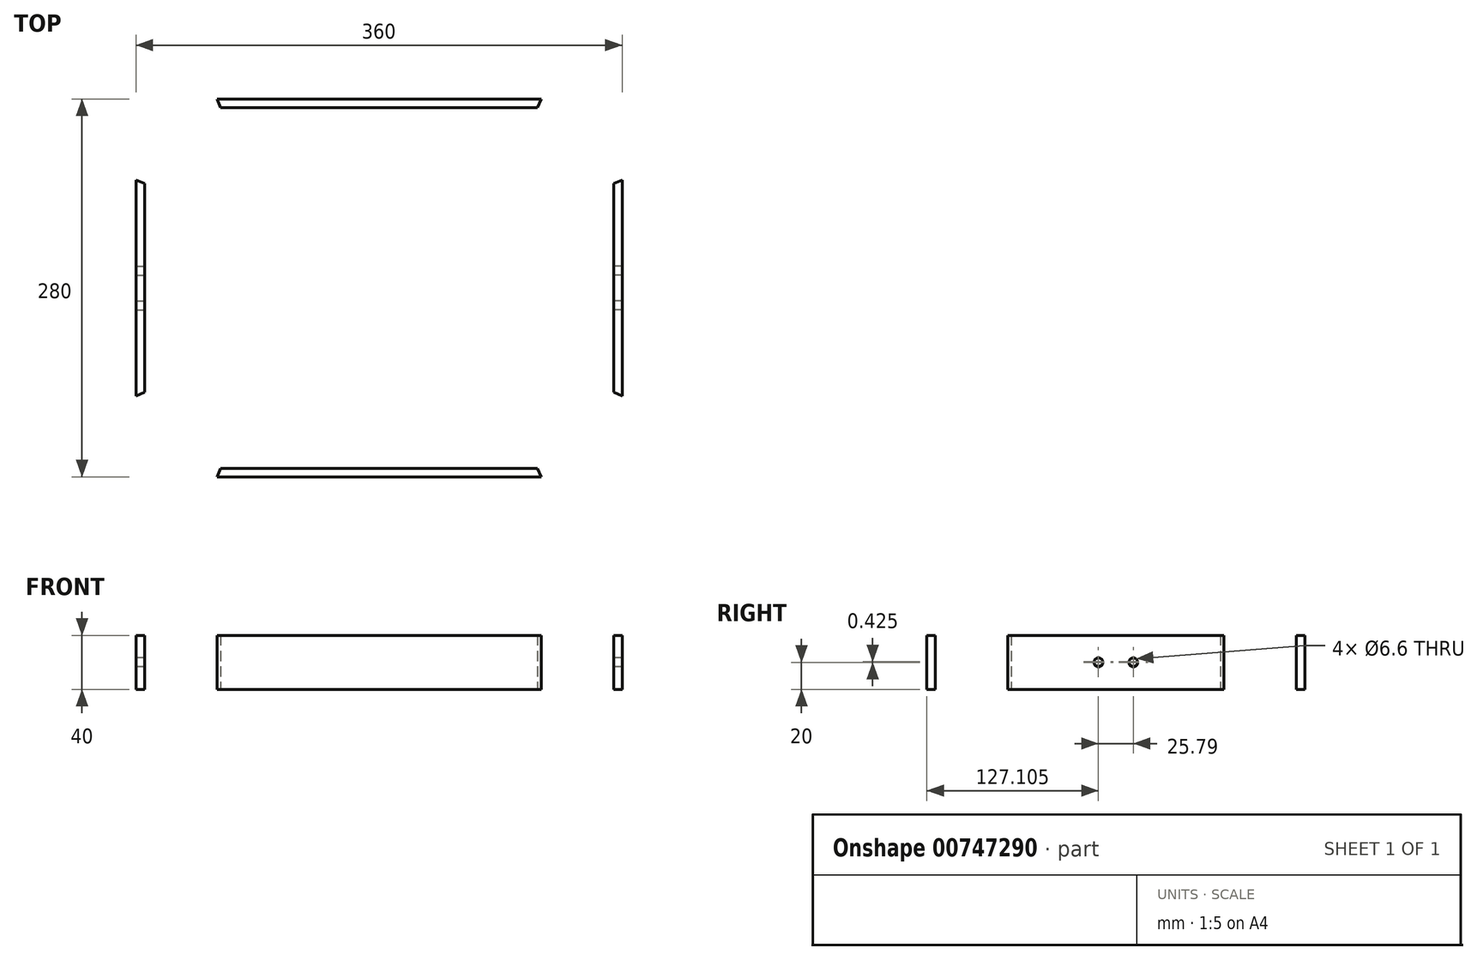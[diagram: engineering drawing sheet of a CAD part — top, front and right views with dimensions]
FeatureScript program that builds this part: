
annotation { "Feature Type Name" : "Feature", "Feature Type Description" : "" }
export const myFeature = defineFeature(function(context is Context, id is Id, definition is map)
    precondition{}
    {
        {
            var Q0;
            Q0=qCreatedBy(makeId("Top.planeOp"),FACE);
            var sketch = newSketch(context, id + "F0", { "sketchPlane" : qUnion([Q0])});
            skLineSegment(sketch, "E0", {"start": v(-120, 0) * mm, "end": v(-180, 60) * mm});
            skLineSegment(sketch, "E1", {"start": v(-180, 60) * mm, "end": v(-180, 220) * mm});
            skLineSegment(sketch, "E2", {"start": v(-180, 220) * mm, "end": v(-120, 280) * mm});
            skLineSegment(sketch, "E3", {"start": v(-120, 280) * mm, "end": v(120, 280) * mm});
            skLineSegment(sketch, "E4", {"start": v(120, 280) * mm, "end": v(180, 220) * mm});
            skLineSegment(sketch, "E5", {"start": v(180, 220) * mm, "end": v(180, 60) * mm});
            skLineSegment(sketch, "E6", {"start": v(180, 60) * mm, "end": v(120, 0) * mm});
            skLineSegment(sketch, "E7", {"start": v(120, 0) * mm, "end": v(-120, 0) * mm});
            skLineSegment(sketch, "E8.0", {"start": v(-173.65, 62.63) * mm, "end": v(-173.65, 217.37) * mm});
            skLineSegment(sketch, "E8.1", {"start": v(-117.37, 6.35) * mm, "end": v(-173.65, 62.63) * mm});
            skLineSegment(sketch, "E8.2", {"start": v(-173.65, 217.37) * mm, "end": v(-117.37, 273.65) * mm});
            skLineSegment(sketch, "E8.3", {"start": v(117.37, 6.35) * mm, "end": v(-117.37, 6.35) * mm});
            skLineSegment(sketch, "E8.4", {"start": v(-117.37, 273.65) * mm, "end": v(117.37, 273.65) * mm});
            skLineSegment(sketch, "E8.5", {"start": v(117.37, 273.65) * mm, "end": v(173.65, 217.37) * mm});
            skLineSegment(sketch, "E8.6", {"start": v(173.65, 217.37) * mm, "end": v(173.65, 62.63) * mm});
            skLineSegment(sketch, "E8.7", {"start": v(173.65, 62.63) * mm, "end": v(117.37, 6.35) * mm});
            skLineSegment(sketch, "E9", {"start": v(-120, 0) * mm, "end": v(-117.37, 6.35) * mm});
            skLineSegment(sketch, "E10", {"start": v(-120, 280) * mm, "end": v(-117.37, 273.65) * mm});
            skLineSegment(sketch, "E11", {"start": v(120, 280) * mm, "end": v(117.37, 273.65) * mm});
            skLineSegment(sketch, "E12", {"start": v(120, 0) * mm, "end": v(117.37, 6.35) * mm});
            skLineSegment(sketch, "E13", {"start": v(-173.65, 217.37) * mm, "end": v(-180, 220) * mm});
            skLineSegment(sketch, "E14", {"start": v(-173.65, 62.63) * mm, "end": v(-180, 60) * mm});
            skLineSegment(sketch, "E15", {"start": v(173.65, 62.63) * mm, "end": v(180, 60) * mm});
            skLineSegment(sketch, "E16", {"start": v(173.65, 217.37) * mm, "end": v(180, 220) * mm});
            skSolve(sketch);
        }
        {
            var Q0;
            Q0=makeQuery(id+"F0.imprint","IMPRINT",FACE,{"disambiguationData":[TD([[makeQuery(id+"F0.imprint","IMPRINT",EDGE,{"derivedFrom":sQuery(id+"F0.wireOp",EDGE,"E3")}),-1.0]])]});
            extrude(context, id + "F1", {"entities" : qUnion([Q0]), "depth" : 40 * mm, "offsetDistance" : 25 * mm});
        }
        {
            var Q0;
            Q0=makeQuery(id+"F0.imprint","IMPRINT",FACE,{"disambiguationData":[TD([[makeQuery(id+"F0.imprint","IMPRINT",EDGE,{"derivedFrom":sQuery(id+"F0.wireOp",EDGE,"E1")}),-1.0]])]});
            extrude(context, id + "F2", {"entities" : qUnion([Q0]), "depth" : 40 * mm, "offsetDistance" : 25 * mm});
        }
        {
            var Q0;
            Q0=makeQuery(id+"F0.imprint","IMPRINT",FACE,{"disambiguationData":[TD([[makeQuery(id+"F0.imprint","IMPRINT",EDGE,{"derivedFrom":sQuery(id+"F0.wireOp",EDGE,"E5")}),-1.0]])]});
            extrude(context, id + "F3", {"entities" : qUnion([Q0]), "depth" : 40 * mm, "offsetDistance" : 25 * mm});
        }
        {
            var Q0;
            Q0=makeQuery(id+"F0.imprint","IMPRINT",FACE,{"disambiguationData":[TD([[makeQuery(id+"F0.imprint","IMPRINT",EDGE,{"derivedFrom":sQuery(id+"F0.wireOp",EDGE,"E7")}),-1.0]])]});
            extrude(context, id + "F4", {"entities" : qUnion([Q0]), "depth" : 40 * mm, "offsetDistance" : 25 * mm});
        }
        {
            var Q0;
            Q0=makeQuery(id+"F2.opExtrude","SWEPT_FACE",FACE,{"disambiguationData":[OSD([sQuery(id+"F0.wireOp",EDGE,"E8.0")])]});
            var sketch = newSketch(context, id + "F5", { "sketchPlane" : qUnion([Q0])});
            skLineSegment(sketch, "E17", {"start": v(140, 40) * mm, "end": v(140, 0) * mm, "construction": true});
            skLineSegment(sketch, "E18.bottom", {"start": v(127.1, 40) * mm, "end": v(152.9, 40) * mm, "construction": true});
            skLineSegment(sketch, "E18.top", {"start": v(127.1, 20.43) * mm, "end": v(152.9, 20.42) * mm, "construction": true});
            skLineSegment(sketch, "E18.left", {"start": v(127.1, 40) * mm, "end": v(127.1, 20.43) * mm, "construction": true});
            skLineSegment(sketch, "E18.right", {"start": v(152.9, 40) * mm, "end": v(152.9, 20.43) * mm, "construction": true});
            skSolve(sketch);
        }
        {
            var Q0;
            Q0=sQuery(id+"F5.wireOp",VERTEX,"E18.top.start");
            var Q1;
            Q1=sQuery(id+"F5.wireOp",VERTEX,"E18.top.end");
            var Q2;
            Q2=makeQuery(id+"F2.opExtrude","SWEPT_BODY",BODY,{"disambiguationData":[OSD([sQuery(id+"F0.wireOp",EDGE,"E1"),sQuery(id+"F0.wireOp",EDGE,"E8.0"),sQuery(id+"F0.wireOp",EDGE,"E13"),sQuery(id+"F0.wireOp",EDGE,"E14")])]});
            hole(context, id + "F6", {"style" : HoleStyle.SIMPLE, "endStyle" : HoleEndStyle.THROUGH, "standardTappedOrClearance" : lookupTablePath({ "standard" : "ISO", "fit" : "Normal", "size" : "M6", "type" : "Clearance" }), "standardBlindInLast" : lookupTablePath({ "fit" : "Standard", "standard" : "ISO", "size" : "M6", "type" : "Clearance" }), "holeDiameter" : 6.6 * mm, "majorDiameter" : 5 * mm, "isTappedThrough" : true, "tappedDepth" : 12 * mm, "tapClearance" : 3, "locations" : qUnion([Q0, Q1]), "scope" : qUnion([Q2])});
        }
        {
            var Q0;
            Q0=makeQuery(id+"F3.opExtrude","SWEPT_FACE",FACE,{"disambiguationData":[OSD([sQuery(id+"F0.wireOp",EDGE,"E8.6")])]});
            var sketch = newSketch(context, id + "F7", { "sketchPlane" : qUnion([Q0])});
            skLineSegment(sketch, "E19", {"start": v(-140, 40) * mm, "end": v(-140, 0) * mm, "construction": true});
            skLineSegment(sketch, "E20.bottom", {"start": v(-152.9, 40) * mm, "end": v(-127.1, 40) * mm, "construction": true});
            skLineSegment(sketch, "E20.top", {"start": v(-152.9, 20) * mm, "end": v(-127.1, 20) * mm, "construction": true});
            skLineSegment(sketch, "E20.left", {"start": v(-152.9, 40) * mm, "end": v(-152.9, 20) * mm, "construction": true});
            skLineSegment(sketch, "E20.right", {"start": v(-127.1, 40) * mm, "end": v(-127.1, 20) * mm, "construction": true});
            skSolve(sketch);
        }
        {
            var Q0;
            Q0=sQuery(id+"F7.wireOp",VERTEX,"E20.right.end");
            var Q1;
            Q1=sQuery(id+"F7.wireOp",VERTEX,"E20.left.end");
            var Q2;
            Q2=makeQuery(id+"F3.opExtrude","SWEPT_BODY",BODY,{"disambiguationData":[OSD([sQuery(id+"F0.wireOp",EDGE,"E5"),sQuery(id+"F0.wireOp",EDGE,"E8.6"),sQuery(id+"F0.wireOp",EDGE,"E15"),sQuery(id+"F0.wireOp",EDGE,"E16")])]});
            hole(context, id + "F8", {"style" : HoleStyle.SIMPLE, "endStyle" : HoleEndStyle.THROUGH, "standardTappedOrClearance" : lookupTablePath({ "standard" : "ISO", "fit" : "Normal", "size" : "M6", "type" : "Clearance" }), "standardBlindInLast" : lookupTablePath({ "fit" : "Standard", "standard" : "ISO", "size" : "M6", "type" : "Clearance" }), "holeDiameter" : 6.6 * mm, "majorDiameter" : 5 * mm, "isTappedThrough" : true, "tappedDepth" : 12 * mm, "tapClearance" : 3, "locations" : qUnion([Q0, Q1]), "scope" : qUnion([Q2])});
        }
    });
